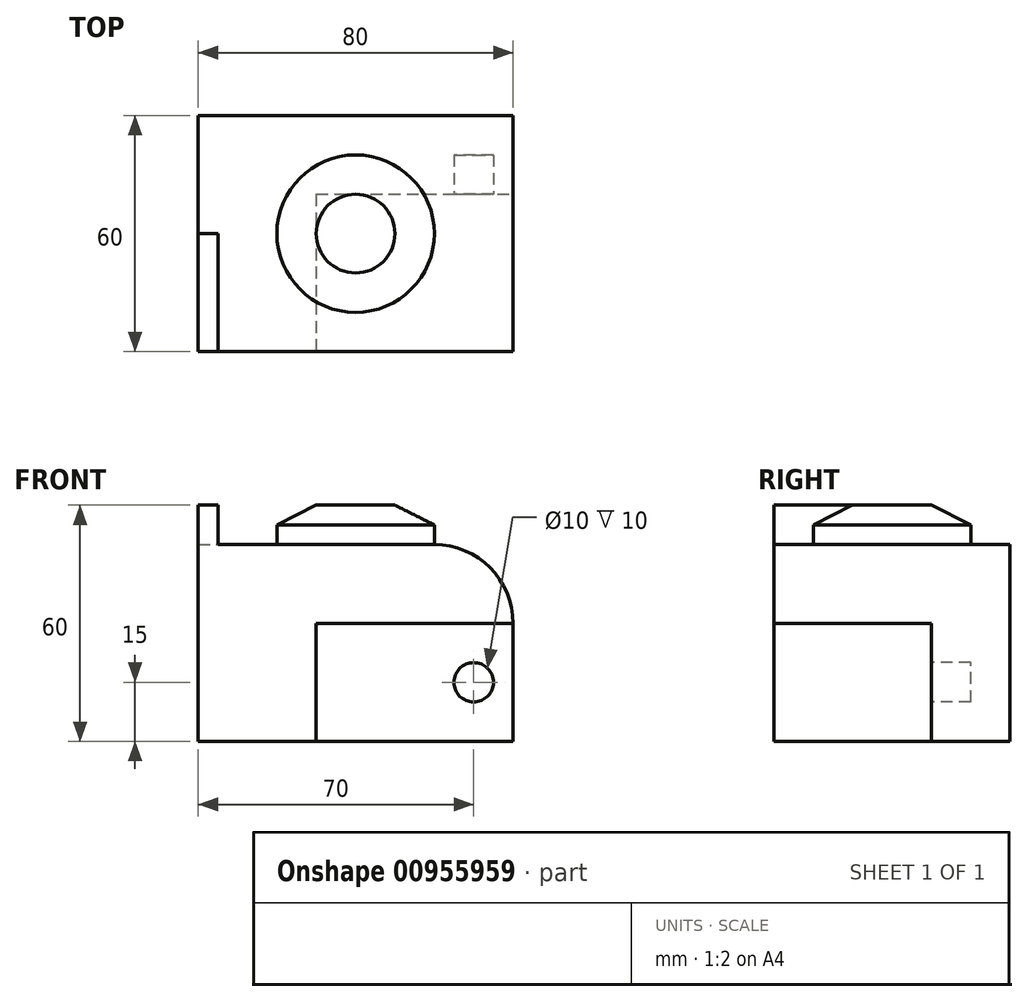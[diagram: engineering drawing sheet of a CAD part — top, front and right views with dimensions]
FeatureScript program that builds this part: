
annotation { "Feature Type Name" : "Feature", "Feature Type Description" : "" }
export const myFeature = defineFeature(function(context is Context, id is Id, definition is map)
    precondition{}
    {
        {
            var Q0;
            Q0=qCreatedBy(makeId("Top.planeOp"),FACE);
            var sketch = newSketch(context, id + "F0", { "sketchPlane" : qUnion([Q0])});
            skLineSegment(sketch, "E0.bottom", {"start": v(0, 0) * mm, "end": v(80, 0) * mm});
            skLineSegment(sketch, "E0.top", {"start": v(0, 60) * mm, "end": v(80, 60) * mm});
            skLineSegment(sketch, "E0.left", {"start": v(0, 0) * mm, "end": v(0, 60) * mm});
            skLineSegment(sketch, "E0.right", {"start": v(80, 0) * mm, "end": v(80, 60) * mm});
            skSolve(sketch);
        }
        {
            var Q0;
            Q0 = qSketchRegion(id + "F0", true);
            extrude(context, id + "F1", {"entities" : qUnion([Q0]), "depth" : 50 * mm, "offsetDistance" : 25 * mm});
        }
        {
            var Q0;
            Q0=makeQuery(id+"F1.opExtrude","CAP_EDGE",EDGE,{"disambiguationData":[OSD([sQuery(id+"F0.wireOp",EDGE,"E0.right")])],"isStart":false});
            fillet(context, id + "F2", {"entities" : qUnion([Q0]), "radius" : 20 * mm, "tangentPropagation" : true, "allowEdgeOverflow" : false});
        }
        {
            var Q0;
            Q0=makeQuery(id+"F1.opExtrude","SWEPT_FACE",FACE,{"disambiguationData":[OSD([sQuery(id+"F0.wireOp",EDGE,"E0.bottom")])]});
            var sketch = newSketch(context, id + "F3", { "sketchPlane" : qUnion([Q0])});
            skLineSegment(sketch, "E1.bottom", {"start": v(0, 50) * mm, "end": v(5, 50) * mm});
            skLineSegment(sketch, "E1.top", {"start": v(0, 60) * mm, "end": v(5, 60) * mm});
            skLineSegment(sketch, "E1.left", {"start": v(0, 50) * mm, "end": v(0, 60) * mm});
            skLineSegment(sketch, "E1.right", {"start": v(5, 50) * mm, "end": v(5, 60) * mm});
            skSolve(sketch);
        }
        {
            var Q0;
            Q0 = qSketchRegion(id + "F3", true);
            extrude(context, id + "F4", {"entities" : qUnion([Q0]), "oppositeDirection" : true, "depth" : 30 * mm, "offsetDistance" : 25 * mm});
        }
        {
            var Q0;
            Q0=makeQuery(id+"F1.opExtrude","SWEPT_BODY",BODY,{"disambiguationData":[OSD([sQuery(id+"F0.wireOp",EDGE,"E0.bottom"),sQuery(id+"F0.wireOp",EDGE,"E0.top"),sQuery(id+"F0.wireOp",EDGE,"E0.left"),sQuery(id+"F0.wireOp",EDGE,"E0.right")])]});
            var Q1;
            Q1=makeQuery(id+"F4.opExtrude","SWEPT_BODY",BODY,{"disambiguationData":[OSD([sQuery(id+"F3.wireOp",EDGE,"E1.bottom"),sQuery(id+"F3.wireOp",EDGE,"E1.top"),sQuery(id+"F3.wireOp",EDGE,"E1.left"),sQuery(id+"F3.wireOp",EDGE,"E1.right")])]});
            booleanBodies(context, id + "F5", {"operationType" : BooleanOperationType.UNION, "tools" : qUnion([Q0, Q1])});
        }
        {
            var Q0;
            Q0=makeQuery(id+"F5.opBoolean","MERGE",FACE,{"derivedFrom":[makeQuery(id+"F1.opExtrude","SWEPT_FACE",FACE,{"disambiguationData":[OSD([sQuery(id+"F0.wireOp",EDGE,"E0.bottom")])]}),makeQuery(id+"F4.opExtrude","CAP_FACE",FACE,{"disambiguationData":[OSD([sQuery(id+"F3.wireOp",EDGE,"E1.bottom"),sQuery(id+"F3.wireOp",EDGE,"E1.top"),sQuery(id+"F3.wireOp",EDGE,"E1.left"),sQuery(id+"F3.wireOp",EDGE,"E1.right")])],"isStart":true})]});
            var sketch = newSketch(context, id + "F6", { "sketchPlane" : qUnion([Q0])});
            skLineSegment(sketch, "E2.bottom", {"start": v(80, 0) * mm, "end": v(30, 0) * mm});
            skLineSegment(sketch, "E2.top", {"start": v(80, 30) * mm, "end": v(30, 30) * mm});
            skLineSegment(sketch, "E2.left", {"start": v(80, 0) * mm, "end": v(80, 30) * mm});
            skLineSegment(sketch, "E2.right", {"start": v(30, 0) * mm, "end": v(30, 30) * mm});
            skSolve(sketch);
        }
        {
            var Q0;
            Q0 = qSketchRegion(id + "F6", true);
            extrude(context, id + "F7", {"entities" : qUnion([Q0]), "operationType" : NewBodyOperationType.REMOVE, "oppositeDirection" : true, "depth" : 40 * mm, "offsetDistance" : 25 * mm});
        }
        {
            var Q0;
            Q0=makeQuery(id+"F7.boolean.opBoolean","COPY",FACE,{"derivedFrom":makeQuery(id+"F7.opExtrude","CAP_FACE",FACE,{"disambiguationData":[OSD([sQuery(id+"F6.wireOp",EDGE,"E2.bottom"),sQuery(id+"F6.wireOp",EDGE,"E2.top"),sQuery(id+"F6.wireOp",EDGE,"E2.left"),sQuery(id+"F6.wireOp",EDGE,"E2.right")])],"isStart":false})});
            var sketch = newSketch(context, id + "F8", { "sketchPlane" : qUnion([Q0])});
            skCircle(sketch, "E3", {"center": v(70, 15) * mm, "radius": 5 * mm});
            skSolve(sketch);
        }
        {
            var Q0;
            Q0 = qSketchRegion(id + "F8", true);
            extrude(context, id + "F9", {"entities" : qUnion([Q0]), "operationType" : NewBodyOperationType.REMOVE, "oppositeDirection" : true, "depth" : 10 * mm, "offsetDistance" : 25 * mm});
        }
        {
            var Q0;
            Q0=makeQuery(id+"F1.opExtrude","CAP_FACE",FACE,{"disambiguationData":[OSD([sQuery(id+"F0.wireOp",EDGE,"E0.bottom"),sQuery(id+"F0.wireOp",EDGE,"E0.top"),sQuery(id+"F0.wireOp",EDGE,"E0.left"),sQuery(id+"F0.wireOp",EDGE,"E0.right")])],"isStart":false});
            var sketch = newSketch(context, id + "F10", { "sketchPlane" : qUnion([Q0])});
            skCircle(sketch, "E4", {"center": v(40, 30) * mm, "radius": 20 * mm});
            skSolve(sketch);
        }
        {
            var Q0;
            Q0 = qSketchRegion(id + "F10", true);
            extrude(context, id + "F11", {"entities" : qUnion([Q0]), "operationType" : NewBodyOperationType.ADD, "depth" : 10 * mm, "offsetDistance" : 25 * mm});
        }
        {
            var Q0;
            Q0=makeQuery(id+"F11.opExtrude","CAP_EDGE",EDGE,{"disambiguationData":[OSD([sQuery(id+"F10.wireOp",EDGE,"E4")])],"isStart":false});
            chamfer(context, id + "F12", {"entities" : qUnion([Q0]), "chamferType" : ChamferType.TWO_OFFSETS, "width1" : 10 * mm, "oppositeDirection" : false, "width2" : 5 * mm, "tangentPropagation" : true});
        }
    });
